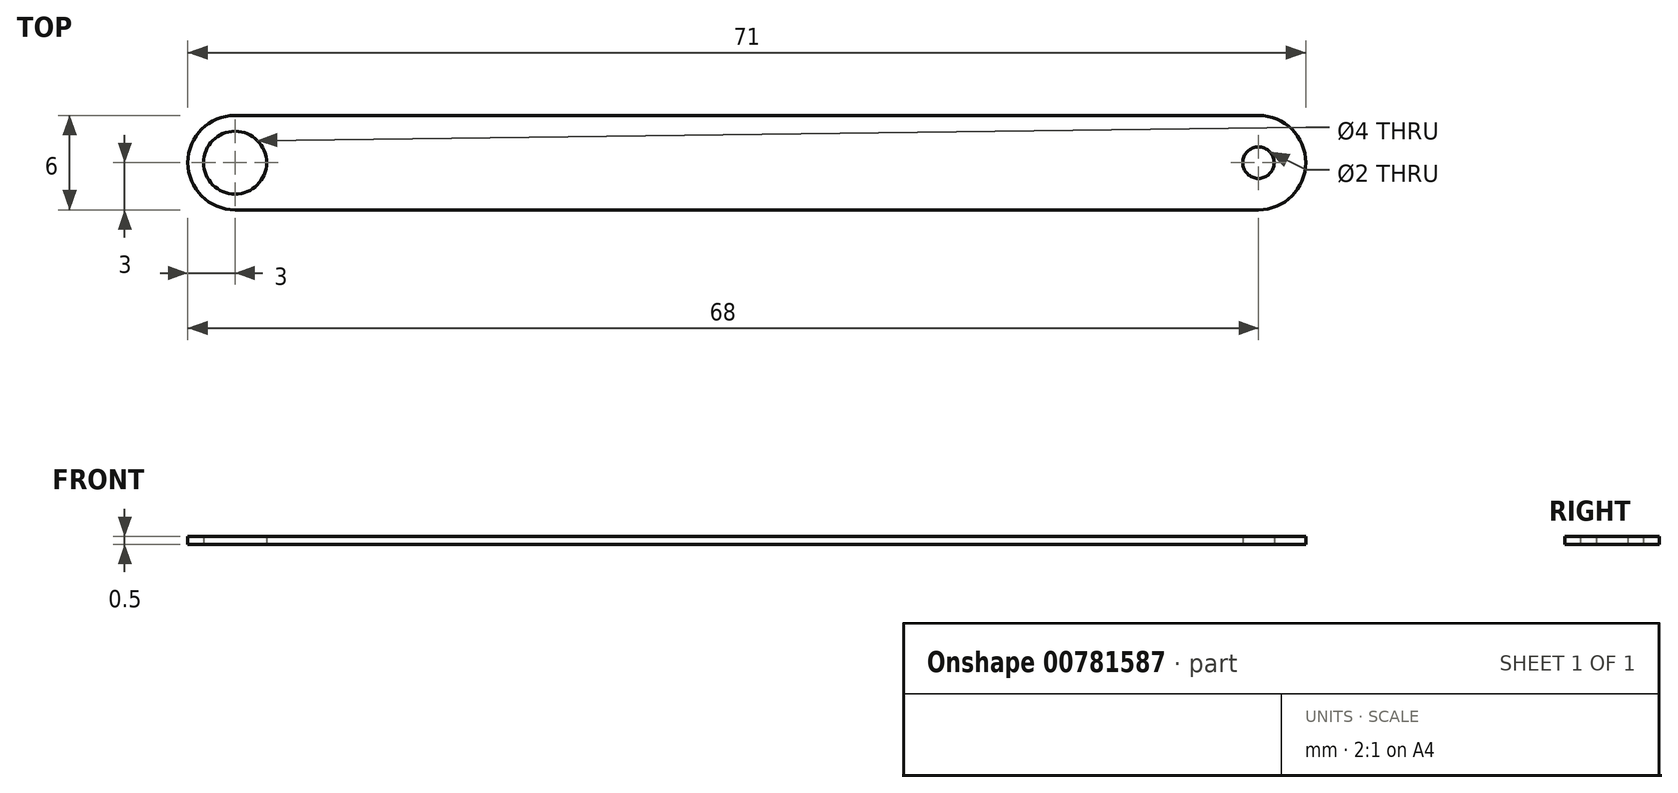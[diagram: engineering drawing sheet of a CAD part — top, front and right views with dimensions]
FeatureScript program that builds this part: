
annotation { "Feature Type Name" : "Feature", "Feature Type Description" : "" }
export const myFeature = defineFeature(function(context is Context, id is Id, definition is map)
    precondition{}
    {
        {
            var Q0;
            Q0=qCreatedBy(makeId("Top.planeOp"),FACE);
            var sketch = newSketch(context, id + "F0", { "sketchPlane" : qUnion([Q0])});
            skLineSegment(sketch, "E0.bottom", {"start": v(-32.5, 0) * mm, "end": v(32.5, 0) * mm});
            skLineSegment(sketch, "E0.top", {"start": v(-32.5, 6) * mm, "end": v(32.5, 6) * mm});
            skLineSegment(sketch, "E0.left", {"start": v(-32.5, 0) * mm, "end": v(-32.5, 6) * mm, "construction": true});
            skLineSegment(sketch, "E0.right", {"start": v(32.5, 0) * mm, "end": v(32.5, 6) * mm, "construction": true});
            skArc(sketch, "E1", {"start": v(32.5, 6) * mm, "mid": v(35.5, 3) * mm, "end": v(32.5, 0) * mm});
            skArc(sketch, "E2", {"start": v(-32.5, 0) * mm, "mid": v(-35.5, 3) * mm, "end": v(-32.5, 6) * mm});
            skCircle(sketch, "E3", {"center": v(-32.5, 3) * mm, "radius": 2 * mm});
            skCircle(sketch, "E4", {"center": v(32.5, 3) * mm, "radius": 1 * mm});
            skSolve(sketch);
        }
        {
            var Q0;
            Q0 = qSketchRegion(id + "F0", true);
            extrude(context, id + "F1", {"entities" : qUnion([Q0]), "endBound" : BoundingType.SYMMETRIC, "depth" : .5 * mm, "offsetDistance" : 25 * mm});
        }
    });
